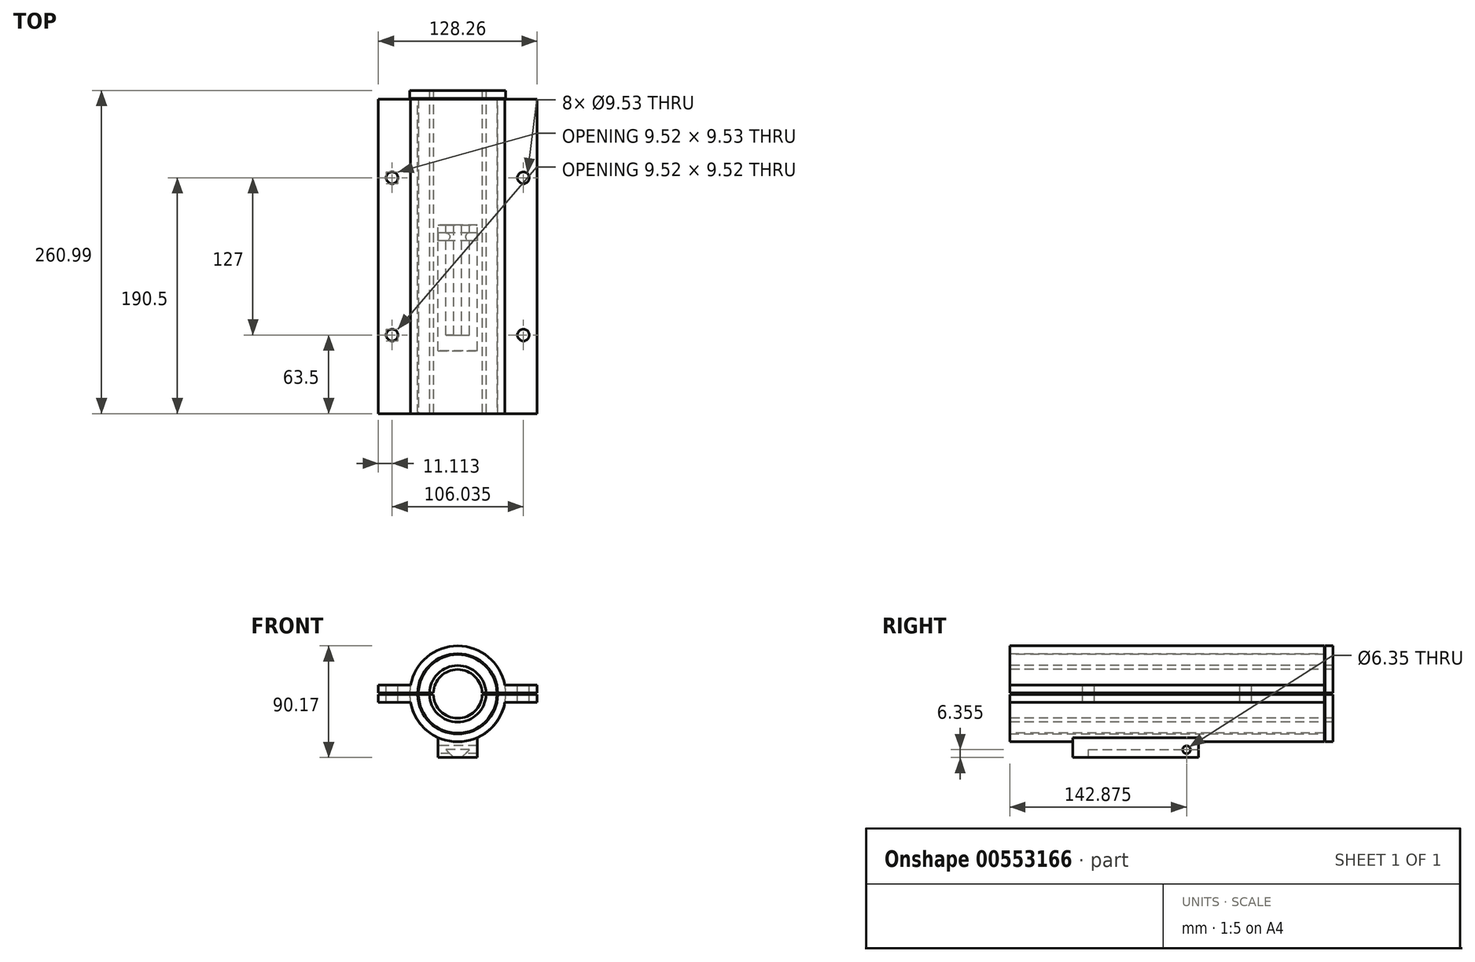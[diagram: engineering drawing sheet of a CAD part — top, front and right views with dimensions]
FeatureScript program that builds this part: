
annotation { "Feature Type Name" : "Feature", "Feature Type Description" : "" }
export const myFeature = defineFeature(function(context is Context, id is Id, definition is map)
    precondition{}
    {
        {
            var Q0;
            Q0=qCreatedBy(makeId("Front.planeOp"),FACE);
            var sketch = newSketch(context, id + "F0", { "sketchPlane" : qUnion([Q0])});
            skArc(sketch, "E0", {"start": v(-31.74, -0.63) * mm, "mid": v(0, -31.75) * mm, "end": v(31.74, -0.63) * mm, "construction": true});
            skLineSegment(sketch, "E1", {"start": v(-64.13, 0) * mm, "end": v(64.13, 0) * mm, "construction": true});
            skLineSegment(sketch, "E2", {"start": v(0, 38.74) * mm, "end": v(0, -38.74) * mm, "construction": true});
            skLineSegment(sketch, "E3.bottom", {"start": v(-64.13, 0.64) * mm, "end": v(-38.73, 0.64) * mm, "construction": true});
            skLineSegment(sketch, "E4.MirrorCS", {"start": v(-64.13, -0.63) * mm, "end": v(-38.73, -0.63) * mm, "construction": true});
            skArc(sketch, "E5", {"start": v(-32.38, -0.63) * mm, "mid": v(0, -32.39) * mm, "end": v(32.38, -0.63) * mm});
            skArc(sketch, "E6", {"start": v(-38.1, -6.99) * mm, "mid": v(0, -38.74) * mm, "end": v(38.1, -6.99) * mm});
            skLineSegment(sketch, "E7", {"start": v(-38.73, 0.64) * mm, "end": v(-64.13, 0.64) * mm});
            skLineSegment(sketch, "E8", {"start": v(-64.13, 0.63) * mm, "end": v(-64.13, 6.99) * mm});
            skLineSegment(sketch, "E9", {"start": v(-64.13, 6.99) * mm, "end": v(-38.1, 6.99) * mm});
            skArc(sketch, "E10.trimOffspring", {"start": v(32.38, 0.63) * mm, "mid": v(0, 32.39) * mm, "end": v(-32.38, 0.63) * mm});
            skArc(sketch, "E11.trimOffspring", {"start": v(31.74, 0.63) * mm, "mid": v(0, 31.75) * mm, "end": v(-31.74, 0.63) * mm, "construction": true});
            skLineSegment(sketch, "E12.trimOffspring", {"start": v(-32.38, 0.64) * mm, "end": v(32.38, 0.64) * mm, "construction": true});
            skLineSegment(sketch, "E13.trimOffspring", {"start": v(-32.38, -0.63) * mm, "end": v(32.38, -0.63) * mm, "construction": true});
            skLineSegment(sketch, "E14.trimOffspring", {"start": v(38.73, 0.64) * mm, "end": v(64.13, 0.63) * mm, "construction": true});
            skLineSegment(sketch, "E15.trimOffspring", {"start": v(38.73, -0.63) * mm, "end": v(64.13, -0.64) * mm, "construction": true});
            skArc(sketch, "E16.trimOffspring", {"start": v(38.1, 6.99) * mm, "mid": v(0, 38.74) * mm, "end": v(-38.1, 6.99) * mm});
            skLineSegment(sketch, "E17", {"start": v(-38.73, 0.64) * mm, "end": v(-32.38, 0.64) * mm});
            skLineSegment(sketch, "E18", {"start": v(-32.38, -0.63) * mm, "end": v(-38.73, -0.63) * mm});
            skLineSegment(sketch, "E19", {"start": v(32.38, -0.63) * mm, "end": v(38.73, -0.63) * mm});
            skLineSegment(sketch, "E20", {"start": v(32.38, 0.64) * mm, "end": v(38.73, 0.64) * mm});
            skLineSegment(sketch, "E21.MirrorCS", {"start": v(38.73, 0.64) * mm, "end": v(64.13, 0.63) * mm});
            skLineSegment(sketch, "E22.MirrorCS", {"start": v(64.13, 6.99) * mm, "end": v(38.1, 6.99) * mm});
            skLineSegment(sketch, "E23.MirrorCS", {"start": v(64.13, 0.63) * mm, "end": v(64.13, 6.99) * mm});
            skLineSegment(sketch, "E24.MirrorCS", {"start": v(-38.73, -0.63) * mm, "end": v(-64.13, -0.63) * mm});
            skLineSegment(sketch, "E25.MirrorCS", {"start": v(-64.13, -0.63) * mm, "end": v(-64.13, -6.99) * mm});
            skLineSegment(sketch, "E26.MirrorCS", {"start": v(-64.13, -6.99) * mm, "end": v(-38.1, -6.99) * mm});
            skLineSegment(sketch, "E27.MirrorCS", {"start": v(38.73, -0.63) * mm, "end": v(64.13, -0.64) * mm});
            skLineSegment(sketch, "E28.MirrorCS", {"start": v(64.13, -0.63) * mm, "end": v(64.13, -6.99) * mm});
            skLineSegment(sketch, "E29.MirrorCS", {"start": v(64.13, -6.99) * mm, "end": v(38.1, -6.99) * mm});
            skSolve(sketch);
        }
        {
            var Q0;
            Q0 = qSketchRegion(id + "F0", true);
            extrude(context, id + "F1", {"entities" : qUnion([Q0]), "depth" : 254 * mm, "offsetDistance" : 25.4 * mm});
        }
        {
            var Q0;
            Q0=makeQuery(id+"F1.opExtrude","SWEPT_FACE",FACE,{"disambiguationData":[OSD([sQuery(id+"F0.wireOp",EDGE,"E19"),sQuery(id+"F0.wireOp",EDGE,"E27.MirrorCS")])]});
            cPlane(context, id + "F2", {"entities" : qUnion([Q0]), "cplaneType" : CPlaneType.OFFSET, "offset" : 50.8 * mm, "oppositeDirection" : true, "width" : 152.4 * mm, "height" : 152.4 * mm});
        }
        {
            var Q0;
            Q0=qCreatedBy(id+"F2.planeOp",FACE);
            var sketch = newSketch(context, id + "F3", { "sketchPlane" : qUnion([Q0])});
            skLineSegment(sketch, "E30", {"start": v(0, 0) * mm, "end": v(0, -254) * mm, "construction": true});
            skLineSegment(sketch, "E31.bottom", {"start": v(-15.87, -203.2) * mm, "end": v(15.88, -203.2) * mm});
            skLineSegment(sketch, "E31.top", {"start": v(-15.88, -101.6) * mm, "end": v(15.87, -101.6) * mm});
            skLineSegment(sketch, "E31.left", {"start": v(-15.87, -203.2) * mm, "end": v(-15.88, -101.6) * mm});
            skLineSegment(sketch, "E31.right", {"start": v(15.88, -203.2) * mm, "end": v(15.87, -101.6) * mm});
            skPoint(sketch, "E31.middle", {"position": v(0, -152.4) * mm});
            skLineSegment(sketch, "E32", {"start": v(0, 0) * mm, "end": v(64.13, 0) * mm, "construction": true});
            skSolve(sketch);
        }
        {
            var Q0;
            Q0 = qSketchRegion(id + "F3", true);
            var Q1;
            Q1=makeQuery(id+"F1.opExtrude","SWEPT_FACE",FACE,{"disambiguationData":[OSD([sQuery(id+"F0.wireOp",EDGE,"E6")])]});
            extrude(context, id + "F4", {"entities" : qUnion([Q0]), "operationType" : NewBodyOperationType.ADD, "endBound" : BoundingType.UP_TO_SURFACE, "depth" : 25.4 * mm, "endBoundEntityFace" : qUnion([Q1]), "offsetDistance" : 25.4 * mm});
        }
        {
            var Q0;
            Q0=makeQuery(id+"F4.opExtrude","SWEPT_FACE",FACE,{"disambiguationData":[OSD([sQuery(id+"F3.wireOp",EDGE,"E31.top")])]});
            var sketch = newSketch(context, id + "F5", { "sketchPlane" : qUnion([Q0])});
            skLineSegment(sketch, "E33", {"start": v(0, 0) * mm, "end": v(0, -51.43) * mm, "construction": true});
            skLineSegment(sketch, "E34", {"start": v(0, -51.43) * mm, "end": v(-3.17, -51.43) * mm});
            skLineSegment(sketch, "E35", {"start": v(-3.17, -51.43) * mm, "end": v(-9.53, -45.08) * mm});
            skLineSegment(sketch, "E36", {"start": v(-9.53, -45.08) * mm, "end": v(0, -45.08) * mm});
            skLineSegment(sketch, "E37.MirrorCS", {"start": v(0, -51.43) * mm, "end": v(3.18, -51.43) * mm});
            skLineSegment(sketch, "E38.MirrorCS", {"start": v(3.18, -51.43) * mm, "end": v(9.53, -45.08) * mm});
            skLineSegment(sketch, "E39.MirrorCS", {"start": v(9.53, -45.08) * mm, "end": v(0, -45.08) * mm});
            skSolve(sketch);
        }
        {
            var Q0;
            Q0 = qSketchRegion(id + "F5", true);
            extrude(context, id + "F6", {"entities" : qUnion([Q0]), "operationType" : NewBodyOperationType.REMOVE, "oppositeDirection" : true, "depth" : 88.9 * mm, "offsetDistance" : 25.4 * mm});
        }
        {
            var Q0;
            Q0=makeQuery(id+"F4.opExtrude","SWEPT_FACE",FACE,{"disambiguationData":[OSD([sQuery(id+"F3.wireOp",EDGE,"E31.left")])]});
            var sketch = newSketch(context, id + "F7", { "sketchPlane" : qUnion([Q0])});
            skLineSegment(sketch, "E40", {"start": v(152.4, -51.43) * mm, "end": v(152.4, -35.33) * mm, "construction": true});
            skLineSegment(sketch, "E41", {"start": v(101.6, -43.38) * mm, "end": v(203.2, -43.38) * mm, "construction": true});
            skCircle(sketch, "E42", {"center": v(111.13, -45.08) * mm, "radius": 3.18 * mm});
            skSolve(sketch);
        }
        {
            var Q0;
            Q0 = qSketchRegion(id + "F7", true);
            extrude(context, id + "F8", {"entities" : qUnion([Q0]), "operationType" : NewBodyOperationType.REMOVE, "endBound" : BoundingType.THROUGH_ALL, "oppositeDirection" : true, "depth" : 25.4 * mm, "offsetDistance" : 25.4 * mm});
        }
        {
            var Q0;
            Q0=makeQuery(id+"F1.opExtrude","SWEPT_FACE",FACE,{"disambiguationData":[OSD([sQuery(id+"F0.wireOp",EDGE,"E22.MirrorCS")])]});
            var sketch = newSketch(context, id + "F9", { "sketchPlane" : qUnion([Q0])});
            skLineSegment(sketch, "E43", {"start": v(0, 0) * mm, "end": v(0, -254) * mm, "construction": true});
            skLineSegment(sketch, "E44", {"start": v(64.13, -127) * mm, "end": v(-64.13, -127) * mm, "construction": true});
            skCircle(sketch, "E45", {"center": v(53.02, -190.5) * mm, "radius": 4.76 * mm});
            skCircle(sketch, "E46.MirrorC", {"center": v(53.02, -63.5) * mm, "radius": 4.76 * mm});
            skCircle(sketch, "E47.MirrorC", {"center": v(-53.02, -190.5) * mm, "radius": 4.76 * mm});
            skCircle(sketch, "E48.MirrorC", {"center": v(-53.02, -63.5) * mm, "radius": 4.76 * mm});
            skSolve(sketch);
        }
        {
            var Q0;
            Q0 = qSketchRegion(id + "F9", true);
            extrude(context, id + "F10", {"entities" : qUnion([Q0]), "operationType" : NewBodyOperationType.REMOVE, "endBound" : BoundingType.THROUGH_ALL, "oppositeDirection" : true, "depth" : 25.4 * mm, "offsetDistance" : 25.4 * mm});
        }
        {
            var Q0;
            Q0=qCreatedBy(makeId("Top.planeOp"),FACE);
            var sketch = newSketch(context, id + "F11", { "sketchPlane" : qUnion([Q0])});
            skLineSegment(sketch, "E49", {"start": v(0, -254) * mm, "end": v(0, 6.99) * mm, "construction": true});
            skLineSegment(sketch, "E50", {"start": v(0, 6.99) * mm, "end": v(22.86, 6.99) * mm, "construction": true});
            skLineSegment(sketch, "E51", {"start": v(22.86, 6.99) * mm, "end": v(38.73, 6.99) * mm});
            skLineSegment(sketch, "E52", {"start": v(38.73, 6.99) * mm, "end": v(38.73, 0.64) * mm});
            skLineSegment(sketch, "E53", {"start": v(38.73, 0.64) * mm, "end": v(31.74, 0.63) * mm});
            skLineSegment(sketch, "E54", {"start": v(31.74, 0.63) * mm, "end": v(31.74, -123.5) * mm});
            skPoint(sketch, "E54.endSnap0", {"position": v(0, -123.5) * mm});
            skLineSegment(sketch, "E55", {"start": v(22.86, 6.99) * mm, "end": v(22.86, -123.5) * mm});
            skLineSegment(sketch, "E56", {"start": v(0, -123.5) * mm, "end": v(64.13, -123.5) * mm, "construction": true});
            skLineSegment(sketch, "E57", {"start": v(22.86, -123.5) * mm, "end": v(22.86, -254) * mm});
            skLineSegment(sketch, "E58", {"start": v(22.86, -254) * mm, "end": v(31.74, -254) * mm});
            skLineSegment(sketch, "E59", {"start": v(31.74, -254) * mm, "end": v(31.74, -123.5) * mm});
            skSolve(sketch);
        }
        {
            var Q0;
            Q0 = qSketchRegion(id + "F11", true);
            var Q1;
            Q1=sQuery(id+"F11.wireOp",EDGE,"E49");
            revolve(context, id + "F12", {"entities" : qUnion([Q0]), "axis" : qUnion([Q1]), "revolveType" : RevolveType.FULL});
        }
        {
            var Q0;
            Q0=qCreatedBy(makeId("Top.planeOp"),FACE);
            var sketch = newSketch(context, id + "F13", { "sketchPlane" : qUnion([Q0])});
            skLineSegment(sketch, "E60", {"start": v(64.13, -254) * mm, "end": v(0, -254) * mm, "construction": true});
            skLineSegment(sketch, "E61", {"start": v(0, -254) * mm, "end": v(0, 6.98) * mm, "construction": true});
            skLineSegment(sketch, "E62", {"start": v(0, 6.98) * mm, "end": v(19.68, 6.98) * mm, "construction": true});
            skLineSegment(sketch, "E63", {"start": v(19.68, 6.98) * mm, "end": v(19.69, -254) * mm});
            skLineSegment(sketch, "E64", {"start": v(19.69, -254) * mm, "end": v(31.74, -254) * mm});
            skLineSegment(sketch, "E65", {"start": v(31.74, -254) * mm, "end": v(31.74, 0.63) * mm});
            skLineSegment(sketch, "E66", {"start": v(31.74, 0.64) * mm, "end": v(38.73, 0.64) * mm});
            skLineSegment(sketch, "E67", {"start": v(38.73, 0.64) * mm, "end": v(38.73, 6.99) * mm});
            skLineSegment(sketch, "E68", {"start": v(38.73, 6.99) * mm, "end": v(19.68, 6.98) * mm});
            skSolve(sketch);
        }
        {
            var Q0;
            Q0 = qSketchRegion(id + "F13", true);
            var Q1;
            Q1=sQuery(id+"F13.wireOp",EDGE,"E61");
            revolve(context, id + "F14", {"entities" : qUnion([Q0]), "axis" : qUnion([Q1]), "revolveType" : RevolveType.FULL});
        }
        {
            var Q0;
            Q0=makeQuery(id+"F12.opRevolve","SWEPT_FACE",FACE,{"disambiguationData":[OSD([sQuery(id+"F11.wireOp",EDGE,"E51")])]});
            var sketch = newSketch(context, id + "F15", { "sketchPlane" : qUnion([Q0])});
            skLineSegment(sketch, "E69.bottom", {"start": v(-64.13, 0.63) * mm, "end": v(64.13, 0.64) * mm});
            skLineSegment(sketch, "E69.top", {"start": v(-64.13, -0.64) * mm, "end": v(64.13, -0.64) * mm});
            skLineSegment(sketch, "E69.left", {"start": v(-64.13, 0.63) * mm, "end": v(-64.13, -0.63) * mm});
            skLineSegment(sketch, "E69.right", {"start": v(64.13, 0.64) * mm, "end": v(64.13, -0.64) * mm});
            skPoint(sketch, "E69.middle", {"position": v(0, 0) * mm});
            skSolve(sketch);
        }
        {
            var Q0;
            Q0 = qSketchRegion(id + "F15", true);
            extrude(context, id + "F16", {"entities" : qUnion([Q0]), "operationType" : NewBodyOperationType.REMOVE, "endBound" : BoundingType.THROUGH_ALL, "oppositeDirection" : true, "depth" : 25.4 * mm, "offsetDistance" : 25.4 * mm});
        }
        {
            var Q0;
            Q0=makeQuery(id+"F14.opRevolve","SWEPT_FACE",FACE,{"disambiguationData":[OSD([sQuery(id+"F13.wireOp",EDGE,"E68")])]});
            var sketch = newSketch(context, id + "F17", { "sketchPlane" : qUnion([Q0])});
            skLineSegment(sketch, "E70.bottom", {"start": v(-64.13, -0.64) * mm, "end": v(64.13, -0.64) * mm});
            skLineSegment(sketch, "E70.top", {"start": v(-64.13, 0.64) * mm, "end": v(64.13, 0.64) * mm});
            skLineSegment(sketch, "E70.left", {"start": v(-64.13, -0.63) * mm, "end": v(-64.13, 0.63) * mm});
            skLineSegment(sketch, "E70.right", {"start": v(64.13, -0.64) * mm, "end": v(64.13, 0.64) * mm});
            skPoint(sketch, "E70.middle", {"position": v(0, 0) * mm});
            skSolve(sketch);
        }
        {
            var Q0;
            Q0 = qSketchRegion(id + "F17", true);
            extrude(context, id + "F18", {"entities" : qUnion([Q0]), "operationType" : NewBodyOperationType.REMOVE, "endBound" : BoundingType.THROUGH_ALL, "oppositeDirection" : true, "depth" : 25.4 * mm, "offsetDistance" : 25.4 * mm});
        }
    });
